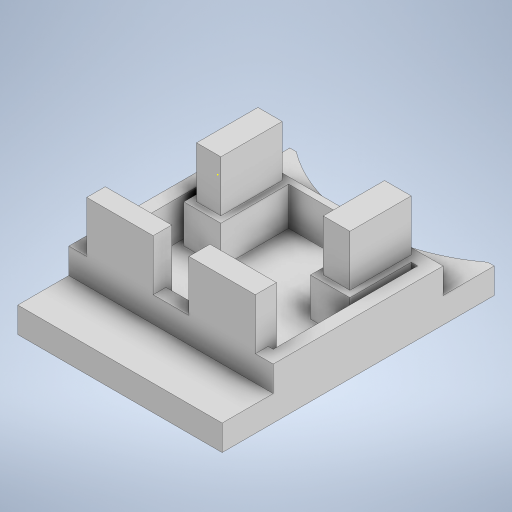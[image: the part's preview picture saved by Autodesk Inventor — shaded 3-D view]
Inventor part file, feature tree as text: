
AUTODESK INVENTOR PART (.ipt)
format: ipt  version: 2024 (Build 280153000, 153)  size: 337,408 bytes
history: native  units: mm
features: extrude x6, sketch x6, projected_geometry x1
ambient origin geometry x8: Origin, YZ Plane, XZ Plane, XY Plane, X Axis, Y Axis, Z Axis, Center Point
bodies: Solid1 (feature_tree)
feature tree (13):
  extrude  "Extrusion1"  Depth=160.0mm
  extrude  "Extrusion2"  Depth=25.0mm
  extrude  "Extrusion3"  Depth=40.0mm TaperAngle=0.0deg
  extrude  "Extrusion4"  Depth=20.0mm
  extrude  "Extrusion5"  Depth=80.0mm
  extrude  "Extrusion6"  Depth=40.0mm TaperAngle=0.0deg
  sketch  "Sketch7"  dims[d13=120.0mm d14=40.0mm d15=0.0mm d16=10.0mm d17=30.0mm d18=0.0mm d19=28.0mm d20=14.0mm d21=14.0mm d22=80.0mm d23=0.0mm d24=52.0mm d25=52.0mm d26=20.0mm d27=40.0mm d28=0.0mm d29=0.0mm d30=40.0mm d31=100.0mm d32=250.0mm d33=100.0mm d34=0.0mm d35=5.0mm]
  sketch  "Sketch1"  dims[d0=133.0mm d1=160.0mm]
  sketch  "Sketch2"  dims[d2=25.0mm d3=25.0mm]
  projected_geometry  "Projected Loop1"
  sketch  "Sketch4"  dims[d4=110.0mm d5=40.0mm d6=0.0mm]
  sketch  "Sketch5"  dims[d7=20.0mm d8=20.0mm]
  sketch  "Sketch6"  dims[d11=80.0mm d12=80.0mm]
